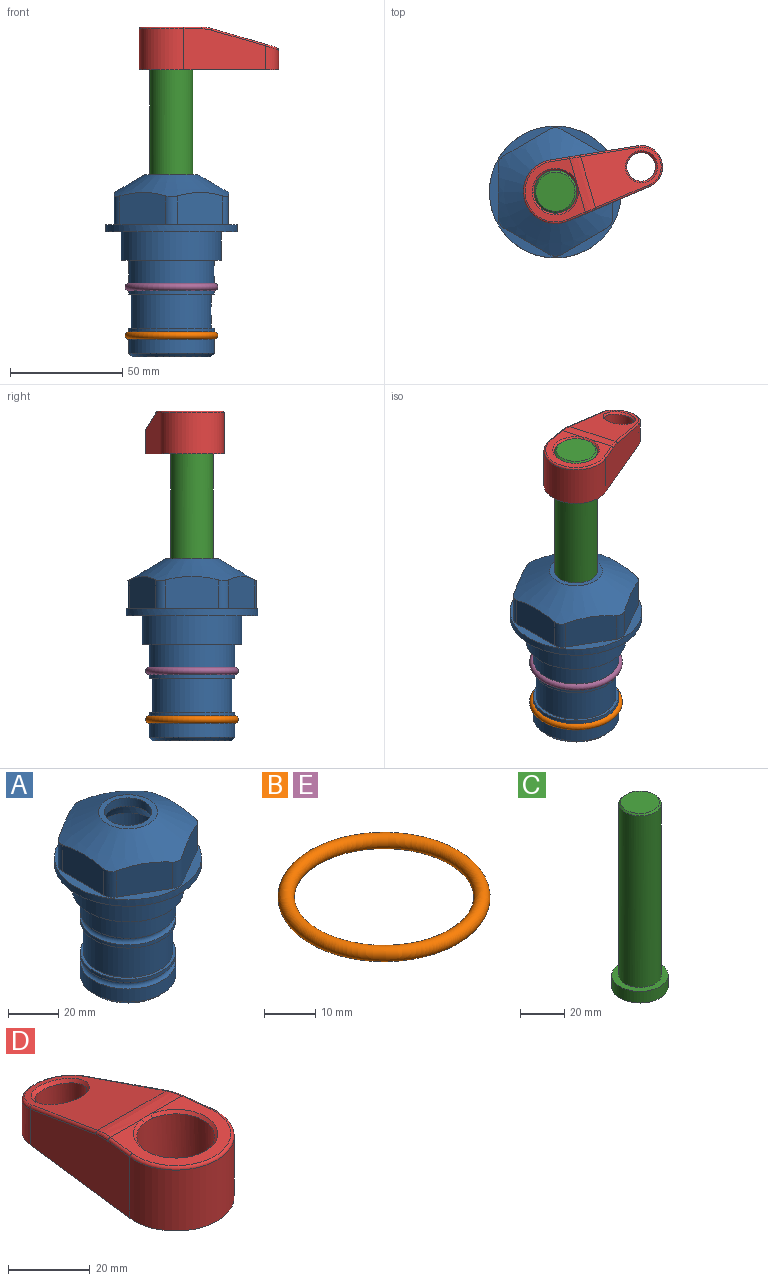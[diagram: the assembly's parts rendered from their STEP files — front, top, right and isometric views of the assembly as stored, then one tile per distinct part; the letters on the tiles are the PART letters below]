
ASSEMBLY  parts=5 mates=4
PART A: 36 faces, bbox 58.7x58.7x81 mm
  f0: cylinder r=17.78mm len=35.56mm, axis (0,0,1), area 1670.8mm2, adj f23,f24,f31
  f1: cylinder r=19.05mm len=38.1mm, axis (0,0,1), area 1191.9mm2, adj f26,f27,f30
  f2: plane 58.66x58.66mm, normal (0,0,-1), area 1150.6mm2, adj f3,f28
  f3: cylinder r=29.33mm len=58.66mm, axis (0,0,-1), area 585.1mm2, adj f2,f4
  f4: plane 58.66x58.66mm, normal (0,0,1), area 475.9mm2, adj f3,f5,f6,f7,f8,f9,f10,f11
  f5: plane 20.32x14.34mm, normal (-0.5,0.87,0), area 324.4mm2, adj f4,f15,f16,f17
  f6: plane 20.32x14.34mm, normal (0.5,0.87,0), area 324.4mm2, adj f4,f14,f15,f17
  f7: plane 23.48x14.34mm, normal (1,0,0), area 324.4mm2, adj f4,f13,f14,f17
  f8: plane 20.32x14.34mm, normal (0.5,-0.87,0), area 324.4mm2, adj f4,f12,f13,f17
  f9: plane 20.32x14.34mm, normal (-0.5,-0.87,0), area 324.4mm2, adj f4,f11,f12,f17
  f10: plane 23.48x14.34mm, normal (-1,0,0), area 324.4mm2, adj f4,f11,f16,f17
  f11: cylinder r=5.08mm len=12.85mm, axis (0,0,-1), area 67.2mm2, adj f4,f9,f10,f17
  f12: cylinder r=5.08mm len=12.85mm, axis (0,0,-1), area 67.2mm2, adj f4,f8,f9,f17
  f13: cylinder r=5.08mm len=12.85mm, axis (0,0,-1), area 67.2mm2, adj f4,f7,f8,f17
  f14: cylinder r=5.08mm len=12.85mm, axis (0,0,-1), area 67.2mm2, adj f4,f6,f7,f17
  f15: cylinder r=5.08mm len=12.85mm, axis (0,0,-1), area 67.2mm2, adj f4,f5,f6,f17
  f16: cylinder r=5.08mm len=12.85mm, axis (0,0,-1), area 67.2mm2, adj f4,f5,f10,f17
  f17: cone r=11.73mm half-angle=60deg, axis (0,0,-1), area 2071.8mm2, adj f5,f6,f7,f8,f9,f10,f11,f12
  f18: plane 23.46x23.46mm, normal (0,0,1), area 147.4mm2, adj f17,f35
  f19: plane 34.93x34.93mm, normal (0,0,-1), area 958mm2, adj f29
  f20: cylinder r=19.05mm len=38.1mm, axis (0,0,1), area 760.1mm2, adj f21,f29
  f21: torus R=19.05mm, axis (0,0,1), area 565.3mm2, adj f20,f22
  f22: cylinder r=19.05mm len=38.1mm, axis (0,0,1), area 190mm2, adj f21,f23
  f23: plane 38.1x38.1mm, normal (0,0,1), area 146.9mm2, adj f0,f22
  f24: plane 38.1x38.1mm, normal (0,0,-1), area 146.9mm2, adj f0,f25
  f25: cylinder r=19.05mm len=38.1mm, axis (0,0,1), area 190mm2, adj f24,f26
  f26: torus R=19.05mm, axis (0,0,1), area 565.3mm2, adj f1,f25
  f27: plane 44.45x44.45mm, normal (0,0,-1), area 411.7mm2, adj f1,f28
  f28: cylinder r=22.23mm len=44.45mm, axis (0,0,1), area 1773.5mm2, adj f2,f27
  f29: cone r=19.05mm half-angle=45deg, axis (0,0,1), area 257.5mm2, adj f19,f20
  f30: cylinder r=3.17mm len=6.75mm, axis (-1,0,0), area 128mm2, adj f1,f33
  f31: cylinder r=3.17mm len=6.35mm, axis (-1,0,0), area 102.5mm2, adj f0,f33
  f32: plane 25.4x25.4mm, normal (0,0,1), area 506.7mm2, adj f33
  f33: cylinder r=12.7mm len=66.42mm, axis (0,0,-1), area 5236.2mm2, adj f30,f31,f32,f34
  f34: cone r=9.53mm half-angle=30deg, axis (0,0,-1), area 443.4mm2, adj f33,f35
  f35: cylinder r=9.53mm len=19.05mm, axis (0,0,-1), area 240.9mm2, adj f18,f34
PART B: 1 faces, bbox 44.7x44.7x3.2 mm
  f0: torus R=19.05mm, axis (0,0,1), area 1193.9mm2
PART C: 6 faces, bbox 25.4x25.4x101.6 mm
  f0: plane 17.46x17.46mm, normal (0,0,1), area 239.5mm2, adj f5
  f1: plane 25.4x25.4mm, normal (0,0,-1), area 506.7mm2, adj f2
  f2: cylinder r=12.7mm len=25.4mm, axis (0,0,1), area 506.7mm2, adj f1,f3
  f3: plane 25.4x25.4mm, normal (0,0,1), area 221.7mm2, adj f2,f4
  f4: cylinder r=9.53mm len=94.46mm, axis (0,0,1), area 5653mm2, adj f3,f5
  f5: cone r=8.73mm half-angle=45deg, axis (0,0,-1), area 64.4mm2, adj f0,f4
PART D: 31 faces, bbox 31.7x65.5x19.8 mm
  f0: plane 39.12x18.26mm, normal (0.99,0.12,0), area 612.2mm2, adj f1,f4,f7,f11,f13,f15
  f1: cylinder r=9.53mm len=18.91mm, axis (0,0,-1), area 296.1mm2, adj f0,f2,f7,f17
  f2: plane 39.12x18.26mm, normal (-0.99,0.12,0), area 612.2mm2, adj f1,f4,f7,f12,f14,f16
  f3: cylinder r=6.35mm len=12.7mm, axis (0,0,-1), area 362.4mm2, adj f7,f18
  f4: cylinder r=14.29mm len=28.58mm, axis (0,0,-1), area 882.2mm2, adj f0,f2,f7,f10
  f5: cylinder r=9.53mm len=19.05mm, axis (0,0,-1), area 1092.6mm2, adj f7,f19,f20
  f6: plane 26.99x23.69mm, normal (0,0,1), area 216.2mm2, adj f9,f10,f11,f12,f19
  f7: plane 63.5x28.58mm, normal (0,0,-1), area 661.8mm2, adj f0,f1,f2,f3,f4,f5,f22,f23
  f8: plane 33.52x23.6mm, normal (0,0.26,0.97), area 486mm2, adj f9,f15,f16,f17,f18
  f9: cylinder r=19.05mm len=24.72mm, axis (1,0,0), area 120.4mm2, adj f6,f8,f13,f14,f20
  f10: torus R=13.49mm, axis (0,0,1), area 59mm2, adj f4,f6,f11,f12
  f11: cylinder r=0.79mm len=8.67mm, axis (0.12,-0.99,0), area 10.8mm2, adj f0,f6,f10,f13
  f12: cylinder r=0.79mm len=8.67mm, axis (0.12,0.99,0), area 10.8mm2, adj f2,f6,f10,f14
  f13: bspline ~4.95x1.42mm, area 6.1mm2, adj f0,f9,f11,f15
  f14: bspline ~4.95x1.42mm, area 6.1mm2, adj f2,f9,f12,f16
  f15: cylinder r=0.79mm len=25.95mm, axis (0.12,-0.96,0.26), area 32.9mm2, adj f0,f8,f13,f17
  f16: cylinder r=0.79mm len=25.95mm, axis (0.12,0.96,-0.26), area 32.9mm2, adj f2,f8,f14,f17
  f17: bspline ~18.91x8.38mm, area 30mm2, adj f1,f8,f15,f16
  f18: bspline ~14.29x14.29mm, area 48.3mm2, adj f3,f8
  f19: cone r=9.53mm half-angle=45deg, axis (0,0,1), area 66.5mm2, adj f5,f6,f20
  f20: bspline ~3.22x0.96mm, area 3.5mm2, adj f5,f9,f19
  f21: plane 2.75x2.72mm, normal (0,0,-1), area 2.9mm2, adj f23,f25,f28
  f22: plane 23.05x15.88mm, normal (-0.99,-0.12,0), area 323.6mm2, adj f7,f25,f26,f27,f28,f29
  f23: plane 23.05x15.88mm, normal (0.99,-0.12,0), area 323.6mm2, adj f7,f21,f25,f27,f28,f30
  f24: cylinder r=9.53mm len=10.69mm, axis (0,0,-1), area 114.7mm2, adj f7,f27,f29,f30
  f25: cylinder r=12.7mm len=20.59mm, axis (0,0,-1), area 381.1mm2, adj f7,f21,f22,f23,f26,f28
  f26: plane 2.75x2.72mm, normal (0,0,-1), area 2.9mm2, adj f22,f25,f28
  f27: plane 19.72x18.37mm, normal (0,-0.26,-0.97), area 291.8mm2, adj f22,f23,f24,f28,f29,f30
  f28: cylinder r=15.88mm len=19.92mm, axis (1,0,0), area 54.8mm2, adj f21,f22,f23,f25,f26,f27
  f29: cylinder r=1.59mm len=11mm, axis (0,0,-1), area 34.7mm2, adj f7,f22,f24,f27
  f30: cylinder r=1.59mm len=11mm, axis (0,0,-1), area 34.7mm2, adj f7,f23,f24,f27
PART E: same geometry as B
PLACE A at identity fixed
PLACE B t=(0,0,-21.59)mm
PLACE C rot(axis=(0,0,-1),73.9deg) t=(0,0,27.55)mm
PLACE D rot(axis=(0,0,-1),73.9deg) t=(0,0,27.55)mm
PLACE E at identity
MATE fastened E.f0 <-> A.f0  axis (0,0,1) through (0,0,-24.51)mm
MATE fastened B.f0 <-> A.f0  axis (0,0,1) through (0,0,-46.1)mm
MATE fastened D.f4 <-> C.f2  axis (0,0,1) through (0,0,91.05)mm
MATE cylindrical A.f0 <-> C.f2  axis (0,0,1) through (0,0,-50.55)mm
